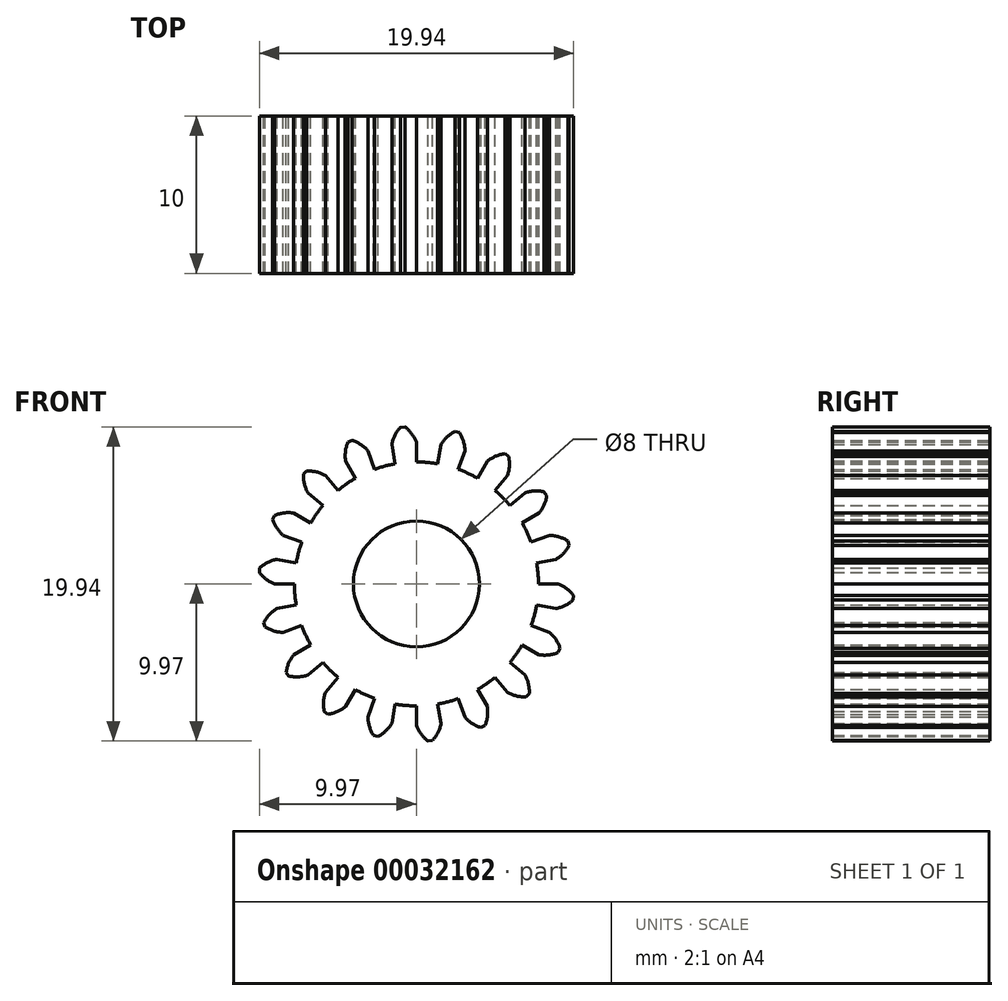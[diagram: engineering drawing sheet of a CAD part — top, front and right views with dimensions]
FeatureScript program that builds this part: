
annotation { "Feature Type Name" : "Feature", "Feature Type Description" : "" }
export const myFeature = defineFeature(function(context is Context, id is Id, definition is map)
    precondition{}
    {
        {
            var Q0;
            Q0=qCreatedBy(makeId("Front.planeOp"),FACE);
            var sketch = newSketch(context, id + "F0", { "sketchPlane" : qUnion([Q0])});
            skArc(sketch, "E0", {"start": v(-1.35, 7.63) * mm, "mid": v(-2, 7.49) * mm, "end": v(-2.65, 7.28) * mm});
            skLineSegment(sketch, "E1", {"start": v(0, 7.75) * mm, "end": v(0, 9) * mm});
            skArc(sketch, "E2", {"start": v(0, 9) * mm, "mid": v(-0.3, 9.54) * mm, "end": v(-0.73, 9.97) * mm});
            skArc(sketch, "E3.0.MirrorCS", {"start": v(-1.56, 8.86) * mm, "mid": v(-1.36, 9.44) * mm, "end": v(-1.02, 9.95) * mm});
            skLineSegment(sketch, "E4.0.MirrorCS", {"start": v(-1.35, 7.63) * mm, "end": v(-1.56, 8.86) * mm});
            skLineSegment(sketch, "E5", {"start": v(-1.02, 9.95) * mm, "end": v(-0.73, 9.97) * mm});
            skPoint(sketch, "E6.orphan", {"position": v(-2.26, 12.8) * mm});
            skPoint(sketch, "E7.orphan", {"position": v(0, 13) * mm});
            skArc(sketch, "E8.1.0", {"start": v(-4.5, 7.8) * mm, "mid": v(-4.51, 8.4) * mm, "end": v(-4.36, 9) * mm});
            skLineSegment(sketch, "E8.1.1", {"start": v(-2.65, 7.28) * mm, "end": v(-3.08, 8.46) * mm});
            skLineSegment(sketch, "E8.1.2", {"start": v(-3.88, 6.71) * mm, "end": v(-4.5, 7.8) * mm});
            skArc(sketch, "E8.1.3", {"start": v(-3.08, 8.46) * mm, "mid": v(-3.54, 8.86) * mm, "end": v(-4.1, 9.12) * mm});
            skLineSegment(sketch, "E8.1.4", {"start": v(-4.36, 9) * mm, "end": v(-4.1, 9.12) * mm});
            skArc(sketch, "E8.2.0", {"start": v(-6.9, 5.79) * mm, "mid": v(-7.11, 6.36) * mm, "end": v(-7.17, 6.97) * mm});
            skLineSegment(sketch, "E8.2.1", {"start": v(-4.98, 5.94) * mm, "end": v(-5.79, 6.9) * mm});
            skLineSegment(sketch, "E8.2.2", {"start": v(-5.94, 4.98) * mm, "end": v(-6.9, 5.79) * mm});
            skArc(sketch, "E8.2.3", {"start": v(-5.79, 6.9) * mm, "mid": v(-6.36, 7.11) * mm, "end": v(-6.97, 7.17) * mm});
            skLineSegment(sketch, "E8.2.4", {"start": v(-7.17, 6.97) * mm, "end": v(-6.97, 7.17) * mm});
            skArc(sketch, "E8.3.0", {"start": v(-8.46, 3.08) * mm, "mid": v(-8.86, 3.54) * mm, "end": v(-9.12, 4.1) * mm});
            skLineSegment(sketch, "E8.3.1", {"start": v(-6.71, 3.88) * mm, "end": v(-7.8, 4.5) * mm});
            skLineSegment(sketch, "E8.3.2", {"start": v(-7.28, 2.65) * mm, "end": v(-8.46, 3.08) * mm});
            skArc(sketch, "E8.3.3", {"start": v(-7.8, 4.5) * mm, "mid": v(-8.4, 4.51) * mm, "end": v(-9, 4.36) * mm});
            skLineSegment(sketch, "E8.3.4", {"start": v(-9.12, 4.1) * mm, "end": v(-9, 4.36) * mm});
            skArc(sketch, "E8.4.0", {"start": v(-9, 0) * mm, "mid": v(-9.54, 0.3) * mm, "end": v(-9.97, 0.73) * mm});
            skLineSegment(sketch, "E8.4.1", {"start": v(-7.63, 1.35) * mm, "end": v(-8.86, 1.56) * mm});
            skLineSegment(sketch, "E8.4.2", {"start": v(-7.75, 0) * mm, "end": v(-9, 0) * mm});
            skArc(sketch, "E8.4.3", {"start": v(-8.86, 1.56) * mm, "mid": v(-9.44, 1.36) * mm, "end": v(-9.95, 1.02) * mm});
            skLineSegment(sketch, "E8.4.4", {"start": v(-9.97, 0.73) * mm, "end": v(-9.95, 1.02) * mm});
            skArc(sketch, "E8.5.0", {"start": v(-8.46, -3.08) * mm, "mid": v(-9.06, -2.98) * mm, "end": v(-9.62, -2.73) * mm});
            skLineSegment(sketch, "E8.5.1", {"start": v(-7.63, -1.35) * mm, "end": v(-8.86, -1.56) * mm});
            skLineSegment(sketch, "E8.5.2", {"start": v(-7.28, -2.65) * mm, "end": v(-8.46, -3.08) * mm});
            skArc(sketch, "E8.5.3", {"start": v(-8.86, -1.56) * mm, "mid": v(-9.34, -1.95) * mm, "end": v(-9.7, -2.45) * mm});
            skLineSegment(sketch, "E8.5.4", {"start": v(-9.62, -2.73) * mm, "end": v(-9.7, -2.45) * mm});
            skArc(sketch, "E8.6.0", {"start": v(-6.9, -5.79) * mm, "mid": v(-7.5, -5.9) * mm, "end": v(-8.1, -5.85) * mm});
            skLineSegment(sketch, "E8.6.1", {"start": v(-6.71, -3.87) * mm, "end": v(-7.8, -4.5) * mm});
            skLineSegment(sketch, "E8.6.2", {"start": v(-5.94, -4.98) * mm, "end": v(-6.9, -5.79) * mm});
            skArc(sketch, "E8.6.3", {"start": v(-7.8, -4.5) * mm, "mid": v(-8.11, -5.03) * mm, "end": v(-8.27, -5.62) * mm});
            skLineSegment(sketch, "E8.6.4", {"start": v(-8.1, -5.85) * mm, "end": v(-8.27, -5.62) * mm});
            skArc(sketch, "E8.7.0", {"start": v(-4.5, -7.8) * mm, "mid": v(-5.03, -8.11) * mm, "end": v(-5.62, -8.27) * mm});
            skLineSegment(sketch, "E8.7.1", {"start": v(-4.98, -5.94) * mm, "end": v(-5.79, -6.9) * mm});
            skLineSegment(sketch, "E8.7.2", {"start": v(-3.87, -6.71) * mm, "end": v(-4.5, -7.8) * mm});
            skArc(sketch, "E8.7.3", {"start": v(-5.79, -6.9) * mm, "mid": v(-5.9, -7.5) * mm, "end": v(-5.85, -8.1) * mm});
            skLineSegment(sketch, "E8.7.4", {"start": v(-5.62, -8.27) * mm, "end": v(-5.85, -8.1) * mm});
            skArc(sketch, "E8.8.0", {"start": v(-1.56, -8.86) * mm, "mid": v(-1.95, -9.34) * mm, "end": v(-2.45, -9.7) * mm});
            skLineSegment(sketch, "E8.8.1", {"start": v(-2.65, -7.28) * mm, "end": v(-3.08, -8.46) * mm});
            skLineSegment(sketch, "E8.8.2", {"start": v(-1.35, -7.63) * mm, "end": v(-1.56, -8.86) * mm});
            skArc(sketch, "E8.8.3", {"start": v(-3.08, -8.46) * mm, "mid": v(-2.98, -9.06) * mm, "end": v(-2.73, -9.62) * mm});
            skLineSegment(sketch, "E8.8.4", {"start": v(-2.45, -9.7) * mm, "end": v(-2.73, -9.62) * mm});
            skArc(sketch, "E8.9.0", {"start": v(1.56, -8.86) * mm, "mid": v(1.36, -9.44) * mm, "end": v(1.02, -9.95) * mm});
            skLineSegment(sketch, "E8.9.1", {"start": v(0, -7.75) * mm, "end": v(0, -9) * mm});
            skLineSegment(sketch, "E8.9.2", {"start": v(1.35, -7.63) * mm, "end": v(1.56, -8.86) * mm});
            skArc(sketch, "E8.9.3", {"start": v(0, -9) * mm, "mid": v(0.3, -9.54) * mm, "end": v(0.73, -9.97) * mm});
            skLineSegment(sketch, "E8.9.4", {"start": v(1.02, -9.95) * mm, "end": v(0.73, -9.97) * mm});
            skArc(sketch, "E8.10.0", {"start": v(4.5, -7.8) * mm, "mid": v(4.51, -8.4) * mm, "end": v(4.36, -9) * mm});
            skLineSegment(sketch, "E8.10.1", {"start": v(2.65, -7.28) * mm, "end": v(3.08, -8.46) * mm});
            skLineSegment(sketch, "E8.10.2", {"start": v(3.88, -6.71) * mm, "end": v(4.5, -7.8) * mm});
            skArc(sketch, "E8.10.3", {"start": v(3.08, -8.46) * mm, "mid": v(3.54, -8.86) * mm, "end": v(4.1, -9.12) * mm});
            skLineSegment(sketch, "E8.10.4", {"start": v(4.36, -9) * mm, "end": v(4.1, -9.12) * mm});
            skArc(sketch, "E8.11.0", {"start": v(6.9, -5.79) * mm, "mid": v(7.11, -6.36) * mm, "end": v(7.17, -6.97) * mm});
            skLineSegment(sketch, "E8.11.1", {"start": v(4.98, -5.94) * mm, "end": v(5.79, -6.9) * mm});
            skLineSegment(sketch, "E8.11.2", {"start": v(5.94, -4.98) * mm, "end": v(6.9, -5.79) * mm});
            skArc(sketch, "E8.11.3", {"start": v(5.79, -6.9) * mm, "mid": v(6.36, -7.11) * mm, "end": v(6.97, -7.17) * mm});
            skLineSegment(sketch, "E8.11.4", {"start": v(7.17, -6.97) * mm, "end": v(6.97, -7.17) * mm});
            skArc(sketch, "E8.12.0", {"start": v(8.46, -3.08) * mm, "mid": v(8.86, -3.54) * mm, "end": v(9.12, -4.1) * mm});
            skLineSegment(sketch, "E8.12.1", {"start": v(6.71, -3.88) * mm, "end": v(7.8, -4.5) * mm});
            skLineSegment(sketch, "E8.12.2", {"start": v(7.28, -2.65) * mm, "end": v(8.46, -3.08) * mm});
            skArc(sketch, "E8.12.3", {"start": v(7.8, -4.5) * mm, "mid": v(8.4, -4.51) * mm, "end": v(9, -4.36) * mm});
            skLineSegment(sketch, "E8.12.4", {"start": v(9.12, -4.1) * mm, "end": v(9, -4.36) * mm});
            skArc(sketch, "E8.13.0", {"start": v(9, 0) * mm, "mid": v(9.54, -0.3) * mm, "end": v(9.97, -0.73) * mm});
            skLineSegment(sketch, "E8.13.1", {"start": v(7.63, -1.35) * mm, "end": v(8.86, -1.56) * mm});
            skLineSegment(sketch, "E8.13.2", {"start": v(7.75, 0) * mm, "end": v(9, 0) * mm});
            skArc(sketch, "E8.13.3", {"start": v(8.86, -1.56) * mm, "mid": v(9.44, -1.36) * mm, "end": v(9.95, -1.02) * mm});
            skLineSegment(sketch, "E8.13.4", {"start": v(9.97, -0.73) * mm, "end": v(9.95, -1.02) * mm});
            skArc(sketch, "E8.14.0", {"start": v(8.46, 3.08) * mm, "mid": v(9.06, 2.98) * mm, "end": v(9.62, 2.73) * mm});
            skLineSegment(sketch, "E8.14.1", {"start": v(7.63, 1.35) * mm, "end": v(8.86, 1.56) * mm});
            skLineSegment(sketch, "E8.14.2", {"start": v(7.28, 2.65) * mm, "end": v(8.46, 3.08) * mm});
            skArc(sketch, "E8.14.3", {"start": v(8.86, 1.56) * mm, "mid": v(9.34, 1.95) * mm, "end": v(9.7, 2.45) * mm});
            skLineSegment(sketch, "E8.14.4", {"start": v(9.62, 2.73) * mm, "end": v(9.7, 2.45) * mm});
            skArc(sketch, "E8.15.0", {"start": v(6.9, 5.79) * mm, "mid": v(7.5, 5.9) * mm, "end": v(8.1, 5.85) * mm});
            skLineSegment(sketch, "E8.15.1", {"start": v(6.71, 3.87) * mm, "end": v(7.8, 4.5) * mm});
            skLineSegment(sketch, "E8.15.2", {"start": v(5.94, 4.98) * mm, "end": v(6.9, 5.79) * mm});
            skArc(sketch, "E8.15.3", {"start": v(7.8, 4.5) * mm, "mid": v(8.11, 5.03) * mm, "end": v(8.27, 5.62) * mm});
            skLineSegment(sketch, "E8.15.4", {"start": v(8.1, 5.85) * mm, "end": v(8.27, 5.62) * mm});
            skArc(sketch, "E8.16.0", {"start": v(4.5, 7.8) * mm, "mid": v(5.03, 8.11) * mm, "end": v(5.62, 8.27) * mm});
            skLineSegment(sketch, "E8.16.1", {"start": v(4.98, 5.94) * mm, "end": v(5.79, 6.9) * mm});
            skLineSegment(sketch, "E8.16.2", {"start": v(3.87, 6.71) * mm, "end": v(4.5, 7.8) * mm});
            skArc(sketch, "E8.16.3", {"start": v(5.79, 6.9) * mm, "mid": v(5.9, 7.5) * mm, "end": v(5.85, 8.1) * mm});
            skLineSegment(sketch, "E8.16.4", {"start": v(5.62, 8.27) * mm, "end": v(5.85, 8.1) * mm});
            skArc(sketch, "E8.17.0", {"start": v(1.56, 8.86) * mm, "mid": v(1.95, 9.34) * mm, "end": v(2.45, 9.7) * mm});
            skLineSegment(sketch, "E8.17.1", {"start": v(2.65, 7.28) * mm, "end": v(3.08, 8.46) * mm});
            skLineSegment(sketch, "E8.17.2", {"start": v(1.35, 7.63) * mm, "end": v(1.56, 8.86) * mm});
            skArc(sketch, "E8.17.3", {"start": v(3.08, 8.46) * mm, "mid": v(2.98, 9.06) * mm, "end": v(2.73, 9.62) * mm});
            skLineSegment(sketch, "E8.17.4", {"start": v(2.45, 9.7) * mm, "end": v(2.73, 9.62) * mm});
            skArc(sketch, "E9.trimOffspring", {"start": v(1.35, 7.63) * mm, "mid": v(0.68, 7.72) * mm, "end": v(0, 7.75) * mm});
            skArc(sketch, "E10.trimOffspring", {"start": v(3.88, 6.71) * mm, "mid": v(3.28, 7.02) * mm, "end": v(2.65, 7.28) * mm});
            skArc(sketch, "E11.trimOffspring", {"start": v(5.94, 4.98) * mm, "mid": v(5.48, 5.48) * mm, "end": v(4.98, 5.94) * mm});
            skArc(sketch, "E12.trimOffspring", {"start": v(7.28, 2.65) * mm, "mid": v(7.02, 3.28) * mm, "end": v(6.71, 3.87) * mm});
            skArc(sketch, "E13.trimOffspring", {"start": v(7.75, 0) * mm, "mid": v(7.72, 0.68) * mm, "end": v(7.63, 1.35) * mm});
            skArc(sketch, "E14.trimOffspring", {"start": v(7.28, -2.65) * mm, "mid": v(7.49, -2) * mm, "end": v(7.63, -1.35) * mm});
            skArc(sketch, "E15.trimOffspring", {"start": v(5.94, -4.98) * mm, "mid": v(6.35, -4.45) * mm, "end": v(6.71, -3.88) * mm});
            skArc(sketch, "E16.trimOffspring", {"start": v(3.87, -6.71) * mm, "mid": v(4.45, -6.35) * mm, "end": v(4.98, -5.94) * mm});
            skArc(sketch, "E17.trimOffspring", {"start": v(1.35, -7.63) * mm, "mid": v(2, -7.49) * mm, "end": v(2.65, -7.28) * mm});
            skArc(sketch, "E18.trimOffspring", {"start": v(-1.35, -7.63) * mm, "mid": v(-0.68, -7.72) * mm, "end": v(0, -7.75) * mm});
            skArc(sketch, "E19.trimOffspring", {"start": v(-3.87, -6.71) * mm, "mid": v(-3.28, -7.02) * mm, "end": v(-2.65, -7.28) * mm});
            skArc(sketch, "E20.trimOffspring", {"start": v(-5.94, -4.98) * mm, "mid": v(-5.48, -5.48) * mm, "end": v(-4.98, -5.94) * mm});
            skArc(sketch, "E21.trimOffspring", {"start": v(-7.28, -2.65) * mm, "mid": v(-7.02, -3.28) * mm, "end": v(-6.71, -3.87) * mm});
            skArc(sketch, "E22.trimOffspring", {"start": v(-7.75, 0) * mm, "mid": v(-7.72, -0.68) * mm, "end": v(-7.63, -1.35) * mm});
            skArc(sketch, "E23.trimOffspring", {"start": v(-7.28, 2.65) * mm, "mid": v(-7.49, 2) * mm, "end": v(-7.63, 1.35) * mm});
            skArc(sketch, "E24.trimOffspring", {"start": v(-5.94, 4.98) * mm, "mid": v(-6.35, 4.45) * mm, "end": v(-6.71, 3.87) * mm});
            skArc(sketch, "E25.trimOffspring", {"start": v(-3.88, 6.71) * mm, "mid": v(-4.45, 6.35) * mm, "end": v(-4.98, 5.94) * mm});
            skCircle(sketch, "E26", {"center": v(0, 0) * mm, "radius": 4 * mm});
            skSolve(sketch);
        }
        {
            var Q0;
            Q0=makeQuery(id+"F0.imprint","IMPRINT",FACE,{"disambiguationData":[TD([[makeQuery(id+"F0.imprint","IMPRINT",EDGE,{"derivedFrom":sQuery(id+"F0.wireOp",EDGE,"E0")}),1.0]])]});
            extrude(context, id + "F1", {"entities" : qUnion([Q0]), "depth" : 10 * mm});
        }
    });
